# Revit family: Lighting_Fixture-Ceiling-Astro-Samos-Round
name_source: partatom
category: Lighting Fixtures
revit_build: Autodesk Revit 2014 (Build: 20130308_1515(x64)
units: mm (PartAtom-declared; Revit-internal decimal feet)

## types (2) — shared parameters
Apparent Load = 6 VA
Assembly Code = D5020200
Class = 2
Color Filter = 16777215
Default Elevation = 1219.2 mm  [stored 4 ft]
Description = Down Light
Dimmable = No
Dimming Lamp Color Temperature Shift = <None>
Energy Efficiency Rating = A+
Height = 31.5 mm  [stored 0.103346 ft]
IP Rating = IP20
Lamp = LED
Lamp included = Yes
Length = 62.5 mm  [stored 0.205052 ft]
Light Source Elevation = 15 mm  [stored 0.0492126 ft]
Luminaire Lamp Efficiency Rating = A+
Manufacturer = Astro Lighting Ltd, CM20 2DP
Mountable on normally flammable surfaces = Yes
Number of Poles = 1
Photometric Web File = 7472 SAMOS ROUND.ies
Suitable for bathroom zone = Zone 3
Tilt Angle = -90.00°
Type Comments = - 230V LED driver not required - Ideal for fitting underneath cabinets
URL = www.astrolighting.co.uk
Voltage = 230 V
Wattage Comments = 5w
Weight = 0.3kg
Width = 62.5 mm  [stored 0.205052 ft]

## per-type parameters (varying)
| type | Casing Material | Model | Product Documentation |
| 5683 Samos Round (Anodised) | Astro - Aluminium - Anodised | 5683 Samos Round Anodised | http://www.astrolighting.co.uk |
| 7472 Samos Round (White) | Astro - Aluminium - White | 7472 Samos Round White | http://wwwhttp: |

note: [stored X ft] marks values corroborated as IEEE doubles in the binary element streams (Revit-internal decimal feet)

## geometry (parser evidence)
native form markers: Sweep x1
no freeform markers — native parametric forms only
